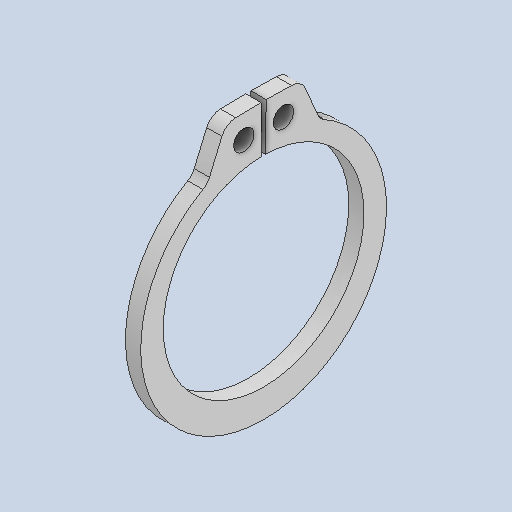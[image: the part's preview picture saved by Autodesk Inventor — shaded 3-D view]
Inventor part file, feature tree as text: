
AUTODESK INVENTOR PART (.ipt)
format: ipt  version: 2023 (Build 270158030, 158C)  size: 102,400 bytes
history: native  units: in
note: dims shown in document units (in); Inventor stores cm internally (conversion verified against a paired STEP export)
features: fillet x1
ambient origin geometry x8: Origin, YZ Plane, XZ Plane, XY Plane, X Axis, Y Axis, Z Axis, Center Point
bodies: Solid1 (feature_tree)
feature tree (1):
  fillet  "Fillet1"  [1 undecoded]
note: 1 required parameter value undecoded (feature->parameter linkage not recoverable at this tier; creation-order binding heuristic only, values carry confidence <= 0.55)
